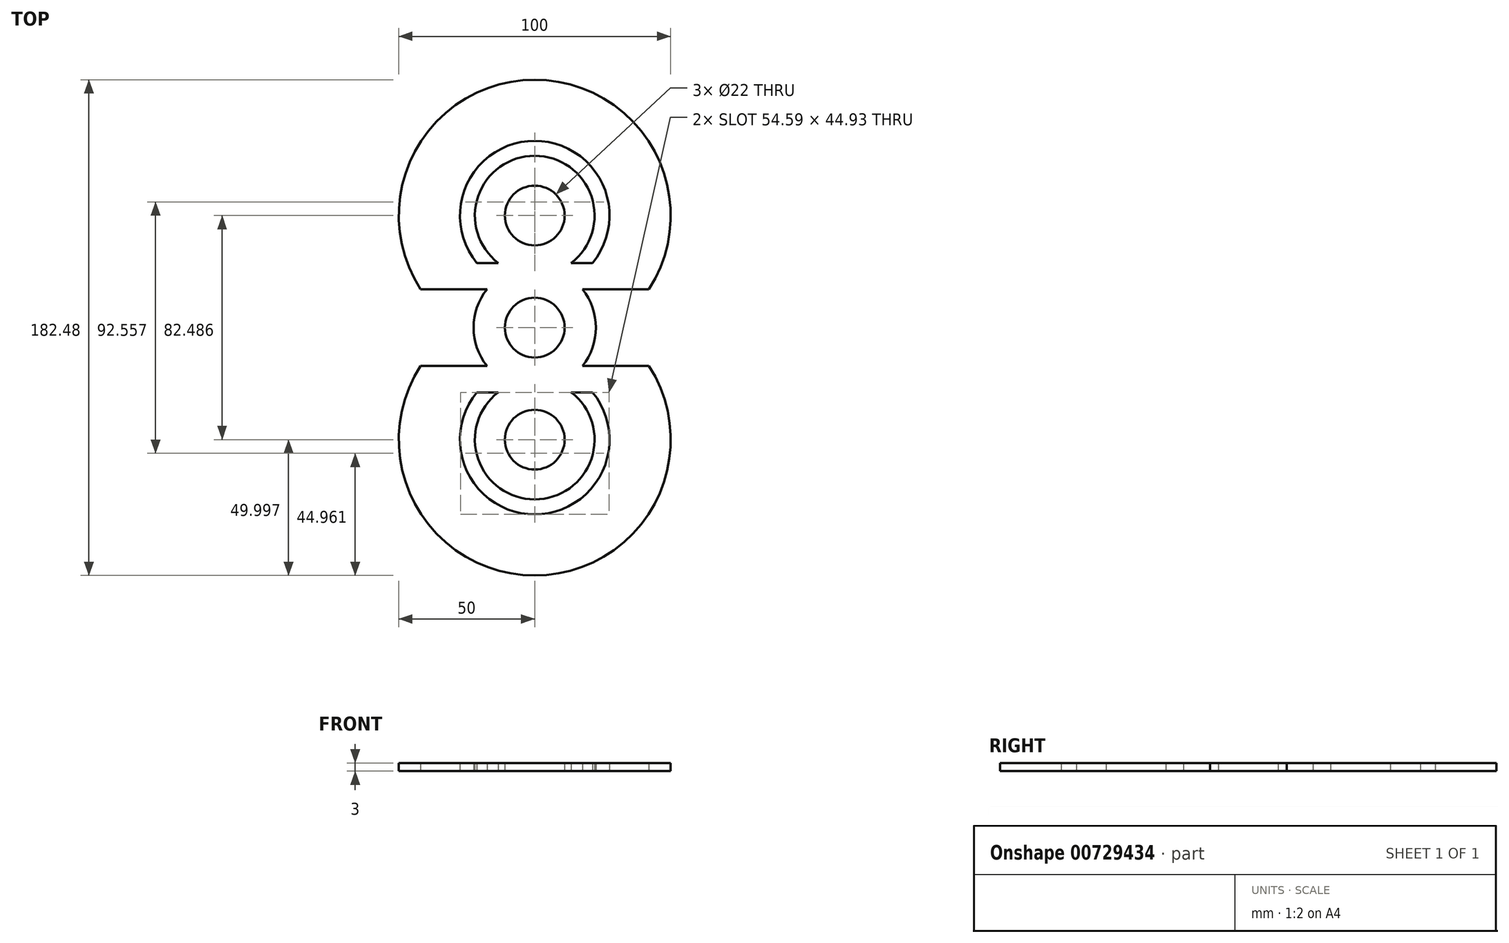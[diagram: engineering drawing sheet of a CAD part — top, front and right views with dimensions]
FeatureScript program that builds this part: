
annotation { "Feature Type Name" : "Feature", "Feature Type Description" : "" }
export const myFeature = defineFeature(function(context is Context, id is Id, definition is map)
    precondition{}
    {
        {
            var Q0;
            Q0=qCreatedBy(makeId("Top.planeOp"),FACE);
            var sketch = newSketch(context, id + "F0", { "sketchPlane" : qUnion([Q0])});
            skArc(sketch, "E0", {"start": v(11, 0) * mm, "mid": v(0, 11) * mm, "end": v(-11, 0) * mm});
            skArc(sketch, "E1", {"start": v(-17.53, 14.1) * mm, "mid": v(-21.22, 7.48) * mm, "end": v(-22.5, 0) * mm});
            skLineSegment(sketch, "E2.0", {"start": v(42, 14.1) * mm, "end": v(17.53, 14.1) * mm});
            skPoint(sketch, "E2.0.midPoint", {"position": v(0, 14.1) * mm});
            skPoint(sketch, "E2.cCircle.center.orphan", {"position": v(0, 41.24) * mm});
            skLineSegment(sketch, "E3.trimOffspring", {"start": v(-17.53, 14.1) * mm, "end": v(-42, 14.1) * mm});
            skArc(sketch, "E4.trimOffspring", {"start": v(22.5, 0) * mm, "mid": v(21.22, 7.48) * mm, "end": v(17.53, 14.1) * mm});
            skArc(sketch, "E5", {"start": v(0, 91.24) * mm, "mid": v(-43.92, 65.15) * mm, "end": v(-42, 14.1) * mm});
            skArc(sketch, "E6", {"start": v(42, 14.1) * mm, "mid": v(43.92, 65.15) * mm, "end": v(0, 91.24) * mm});
            skCircle(sketch, "E7", {"center": v(0, 41.24) * mm, "radius": 11 * mm});
            skArc(sketch, "E8", {"start": v(13.43, 23.81) * mm, "mid": v(0, 63.24) * mm, "end": v(-13.43, 23.81) * mm});
            skArc(sketch, "E9", {"start": v(21.27, 23.81) * mm, "mid": v(0, 68.74) * mm, "end": v(-21.27, 23.81) * mm});
            skLineSegment(sketch, "E10", {"start": v(-21.27, 23.81) * mm, "end": v(-13.43, 23.81) * mm});
            skLineSegment(sketch, "E11.trimOffspring", {"start": v(13.43, 23.81) * mm, "end": v(21.27, 23.81) * mm});
            skLineSegment(sketch, "E12.MirrorCS", {"start": v(-21.27, -23.81) * mm, "end": v(-13.43, -23.81) * mm});
            skLineSegment(sketch, "E13.MirrorCS", {"start": v(13.43, -23.81) * mm, "end": v(21.27, -23.81) * mm});
            skArc(sketch, "E14.MirrorCS", {"start": v(42, -14.1) * mm, "mid": v(43.92, -65.15) * mm, "end": v(0, -91.24) * mm});
            skCircle(sketch, "E15.MirrorC", {"center": v(0, -41.24) * mm, "radius": 11 * mm});
            skLineSegment(sketch, "E16.MirrorCS", {"start": v(42, -14.1) * mm, "end": v(17.53, -14.1) * mm});
            skArc(sketch, "E17.MirrorCS", {"start": v(22.5, 0) * mm, "mid": v(21.22, -7.48) * mm, "end": v(17.53, -14.1) * mm});
            skLineSegment(sketch, "E18.MirrorCS", {"start": v(-17.53, -14.1) * mm, "end": v(-42, -14.1) * mm});
            skArc(sketch, "E19.MirrorCS", {"start": v(0, -91.24) * mm, "mid": v(-43.92, -65.15) * mm, "end": v(-42, -14.1) * mm});
            skArc(sketch, "E20.MirrorCS", {"start": v(-17.53, -14.1) * mm, "mid": v(-21.22, -7.48) * mm, "end": v(-22.5, 0) * mm});
            skArc(sketch, "E21.MirrorCS", {"start": v(13.43, -23.81) * mm, "mid": v(0, -63.24) * mm, "end": v(-13.43, -23.81) * mm});
            skPoint(sketch, "E22.MirrorP", {"position": v(0, -14.1) * mm});
            skArc(sketch, "E23.MirrorCS", {"start": v(11, 0) * mm, "mid": v(0, -11) * mm, "end": v(-11, 0) * mm});
            skArc(sketch, "E24.MirrorCS", {"start": v(21.27, -23.81) * mm, "mid": v(0, -68.74) * mm, "end": v(-21.27, -23.81) * mm});
            skSolve(sketch);
        }
        {
            var Q0;
            Q0 = qSketchRegion(id + "F0", true);
            extrude(context, id + "F1", {"entities" : qUnion([Q0]), "depth" : 3 * mm, "offsetDistance" : 25 * mm});
        }
    });
